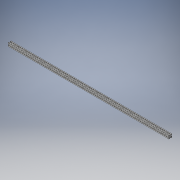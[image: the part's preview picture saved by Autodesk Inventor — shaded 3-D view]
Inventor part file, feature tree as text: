
AUTODESK INVENTOR PART (.ipt)
format: ipt  version: 2019 (Build 230136000, 136)  size: 172,544 bytes
history: native  units: in
note: dims shown in document units (in); Inventor stores cm internally (conversion verified against a paired STEP export)
features: extrude x1, fillet x1, sketch x1
ambient origin geometry x8: Origin, YZ Plane, XZ Plane, XY Plane, X Axis, Y Axis, Z Axis, Center Point
bodies: Solid1 (feature_tree)
feature tree (3):
  extrude  "Extrusion1"  Depth=0.0492in
  fillet  "Fillet1"  [1 undecoded]
  sketch  "Sketch1"  dims[d0=0.1969in d3=0.1417in d4=45.0deg d5=0.122in d7=0.2165in d8=0.063in d11=0.1693in d12=39.3701in d13=0.0in d14=0.0492in]
note: 1 required parameter value undecoded (feature->parameter linkage not recoverable at this tier; creation-order binding heuristic only, values carry confidence <= 0.55)
